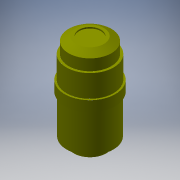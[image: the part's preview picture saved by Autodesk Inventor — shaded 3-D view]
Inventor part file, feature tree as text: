
AUTODESK INVENTOR PART (.ipt)
format: ipt  version: 2016 (Build 200138000, 138)  size: 160,768 bytes
history: native  units: mm
features: sketch x9, extrude x7, plane x1, loft x1, other x1
ambient origin geometry x8: Origin, YZ Plane, XZ Plane, XY Plane, X Axis, Y Axis, Z Axis, Center Point
bodies: Solid1 (feature_tree)
feature tree (19):
  extrude  "Extrusion1"  Depth=5.3mm TaperAngle=0.0deg
  extrude  "Extrusion2"  Depth=29.8mm TaperAngle=0.0deg
  extrude  "Extrusion3"  Depth=8.0mm TaperAngle=0.0deg
  extrude  "Extrusion4"  Depth=17.2mm TaperAngle=0.0deg
  extrude  "Extrusion5"  Depth=1.8mm TaperAngle=0.0deg
  extrude  "Extrusion6"  Depth=6.8mm TaperAngle=0.0deg
  sketch  "Sketch7"  dims[d18=32.9mm d19=3.4mm]
  plane  "Work Plane1"
  loft  "Loft1"
  extrude  "Extrusion7"  TaperAngle=0.0deg  [1 undecoded]
  sketch  "Sketch1"  dims[d0=25.0mm d1=5.3mm d2=0.0mm]
  sketch  "Sketch2"  dims[d3=36.0mm d4=29.8mm d5=0.0mm]
  sketch  "Sketch3"  dims[d6=39.0mm d7=8.0mm d8=0.0mm]
  sketch  "Sketch4"  dims[d9=36.4mm d10=17.2mm d11=0.0mm]
  sketch  "Sketch5"  dims[d12=32.9mm d13=1.8mm d14=0.0mm]
  sketch  "Sketch6"  dims[d15=32.9mm d16=6.8mm d17=0.0mm]
  sketch  "Sketch8"  dims[d20=21.5mm d21=0.0mm d22=90.0deg]
  other  "Edges1"
  sketch  "Sketch9"  dims[d23=0.0mm d24=90.0deg d25=16.9mm d26=1.0mm d27=0.0mm]
note: 1 required parameter value undecoded (feature->parameter linkage not recoverable at this tier; creation-order binding heuristic only, values carry confidence <= 0.55)
